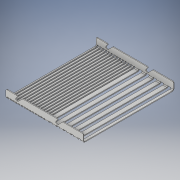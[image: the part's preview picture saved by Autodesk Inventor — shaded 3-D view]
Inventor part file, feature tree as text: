
AUTODESK INVENTOR PART (.ipt)
format: ipt  version: 2018 (Build 220112000, 112)  size: 587,264 bytes
history: native  units: mm
features: other x17, reference x8, sketch x4, fillet x3, extrude x2
ambient origin geometry x8: Origin, YZ Plane, XZ Plane, XY Plane, X Axis, Y Axis, Z Axis, Center Point
bodies: Volumenkörper1 (feature_tree)
feature tree (34):
  other  "Fläche1"
  other  "Lasche2"
  extrude  "Extrusion1"  TaperAngle=0.0deg  [1 undecoded]
  fillet  "Rundung1"  Radius=15.0mm
  fillet  "Rundung2"  Radius=50.0mm
  extrude  "Extrusion2"  Depth=2.0mm
  fillet  "Rundung3"  Radius=1.0mm
  sketch  "Skizze1"  dims[d0=0.0mm d1=0.0mm d2=15.0mm d3=50.0mm]
  reference  "Referenz1"
  reference  "Referenz2"
  reference  "Referenz3"
  reference  "Referenz4"
  reference  "Referenz5"
  reference  "Referenz6"
  other  "Grobblech1"
  sketch  "Skizze3"  dims[d4=2.0mm d15=2.0mm d16=1.0mm]
  other  "Grobblech3"
  other  "Biegung2"
  other  "Ecke2"
  sketch  "Skizze4"  dims[d17=4.0mm]
  reference  "Referenz7"
  reference  "Referenz8"
  sketch  "Skizze5"  dims[d18=2.0mm d19=20.0mm d20=90.0deg d21=2.0mm d22=8.0mm d23=2.0mm d24=2.0mm d25=0.15mm d26=45.0deg d27=45.0deg d28=59.700351mm d29=10.0mm d30=0.0mm d31=2.0mm d32=2.0mm d33=5.0mm d34=3.0mm d35=0.0mm d36=3.0mm d37=100.0mm d39=7.0mm d40=10.0mm d42=10.0mm d44=50.0mm d46=7.0mm d47=10.0mm d49=10.0mm d51=5.0mm d52=8.0mm d53=0.0mm d54=10.0mm d55=50.0mm d57=18.0mm d58=10.0mm d60=10.0mm d62=10.0mm d63=0.0mm d64=2.0mm]
  parser-record x1  (decoder bookkeeping rows leaked as tree rows — omitted from the tree; the rows remain in map.json)
  other  "Montiert.iam"
  other  "Gegenhalter:1"
  other  "Distanzhülse_M4x20:3"
  other  "Distanzhülse_M4x20:5"
  other  "Distanzhülse_M4x20:6"
  other  "Distanzhülse_M4x20:2"
  other  "Boden:1"
  other  "Distanzhülse_M4x20:8"
  other  "Distanzhülse_M4x20:7"
  other  "Definition1"
note: 1 required parameter value undecoded (feature->parameter linkage not recoverable at this tier; creation-order binding heuristic only, values carry confidence <= 0.55)
note: 1 file-system path scrubbed to <path> (originals preserved in map.json)
